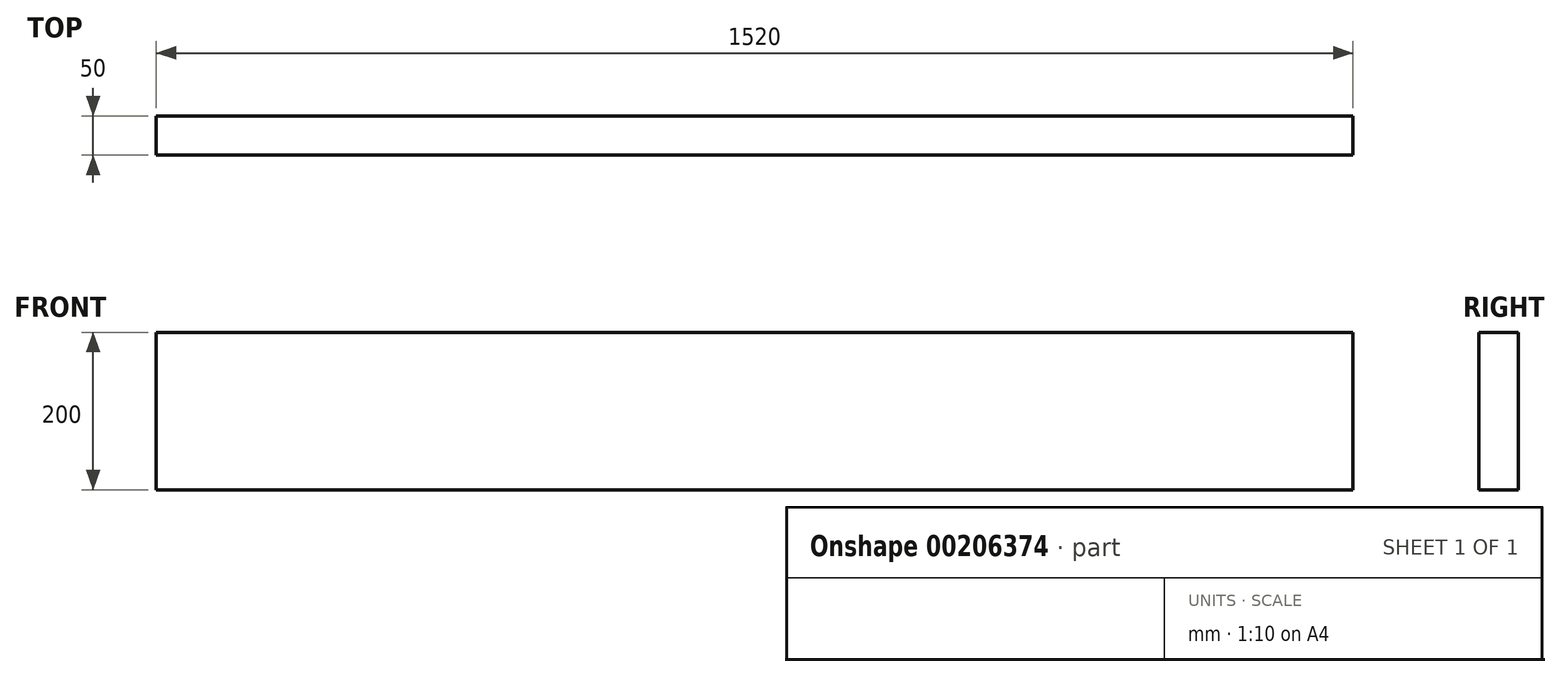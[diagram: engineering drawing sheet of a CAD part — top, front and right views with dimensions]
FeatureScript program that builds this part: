
annotation { "Feature Type Name" : "Feature", "Feature Type Description" : "" }
export const myFeature = defineFeature(function(context is Context, id is Id, definition is map)
    precondition{}
    {
        {
            var Q0;
            Q0=qCreatedBy(makeId("Top.planeOp"),FACE);
            var sketch = newSketch(context, id + "F0", { "sketchPlane" : qUnion([Q0])});
            skLineSegment(sketch, "E0.bottom", {"start": v(-61.6, 19.35) * mm, "end": v(1458.4, 19.35) * mm});
            skLineSegment(sketch, "E0.top", {"start": v(-61.6, -30.65) * mm, "end": v(1458.4, -30.65) * mm});
            skLineSegment(sketch, "E0.left", {"start": v(-61.6, 19.35) * mm, "end": v(-61.6, -30.65) * mm});
            skLineSegment(sketch, "E0.right", {"start": v(1458.4, 19.35) * mm, "end": v(1458.4, -30.65) * mm});
            skSolve(sketch);
        }
        {
            var Q0;
            Q0=makeQuery(id+"F0.imprint","IMPRINT",FACE,{"disambiguationData":[TD([[makeQuery(id+"F0.imprint","IMPRINT",EDGE,{"derivedFrom":sQuery(id+"F0.wireOp",EDGE,"E0.bottom")}),-1.0]])]});
            extrude(context, id + "F1", {"entities" : qUnion([Q0]), "depth" : 200 * mm});
        }
    });
